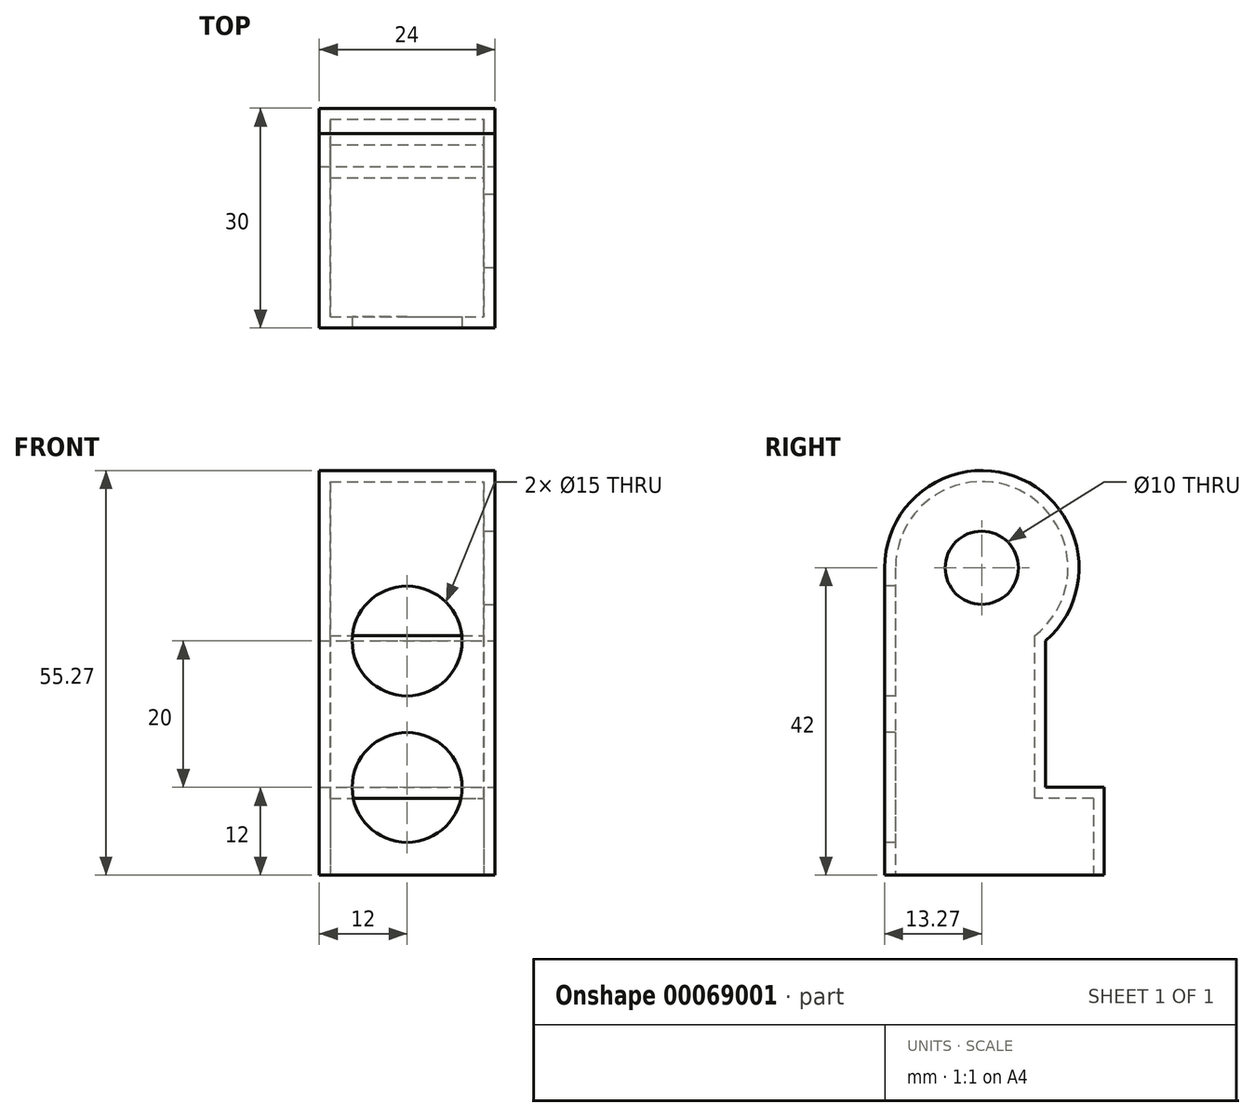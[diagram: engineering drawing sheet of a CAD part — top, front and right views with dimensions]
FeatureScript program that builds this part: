
annotation { "Feature Type Name" : "Feature", "Feature Type Description" : "" }
export const myFeature = defineFeature(function(context is Context, id is Id, definition is map)
    precondition{}
    {
        {
            var Q0;
            Q0=qCreatedBy(makeId("Right.planeOp"),FACE);
            var sketch = newSketch(context, id + "F0", { "sketchPlane" : qUnion([Q0])});
            skArc(sketch, "E0", {"start": v(8.73, -10) * mm, "mid": v(5.5, 12.08) * mm, "end": v(-13.27, 0) * mm});
            skLineSegment(sketch, "E1", {"start": v(-13.27, 0) * mm, "end": v(-13.27, -42) * mm});
            skLineSegment(sketch, "E2", {"start": v(-13.27, -42) * mm, "end": v(16.73, -42) * mm});
            skLineSegment(sketch, "E3", {"start": v(16.73, -30) * mm, "end": v(16.73, -42) * mm});
            skLineSegment(sketch, "E4", {"start": v(16.73, -30) * mm, "end": v(8.73, -30) * mm});
            skLineSegment(sketch, "E5", {"start": v(8.73, -30) * mm, "end": v(8.73, -10) * mm});
            skSolve(sketch);
        }
        {
            var Q0;
            Q0=makeQuery(id+"F0.imprint","IMPRINT",FACE,{"disambiguationData":[TD([[makeQuery(id+"F0.imprint","IMPRINT",EDGE,{"derivedFrom":sQuery(id+"F0.wireOp",EDGE,"E0")}),1.0]])]});
            extrude(context, id + "F1", {"entities" : qUnion([Q0]), "depth" : 24 * mm});
        }
        {
            var Q0;
            Q0=makeQuery(id+"F1.opExtrude","SWEPT_FACE",FACE,{"disambiguationData":[OSD([sQuery(id+"F0.wireOp",EDGE,"E2")])]});
            shell(context, id + "F2", {"entities" : qUnion([Q0]), "thickness" : 1.5 * mm});
        }
        {
            var Q0;
            Q0=makeQuery(id+"F1.opExtrude","CAP_FACE",FACE,{"disambiguationData":[OSD([sQuery(id+"F0.wireOp",EDGE,"E0"),sQuery(id+"F0.wireOp",EDGE,"E1"),sQuery(id+"F0.wireOp",EDGE,"E2"),sQuery(id+"F0.wireOp",EDGE,"E3"),sQuery(id+"F0.wireOp",EDGE,"E4"),sQuery(id+"F0.wireOp",EDGE,"E5")])],"isStart":true});
            var sketch = newSketch(context, id + "F3", { "sketchPlane" : qUnion([Q0])});
            skCircle(sketch, "E6", {"center": v(0, 0) * mm, "radius": 5 * mm});
            skSolve(sketch);
        }
        {
            var Q0;
            Q0=qSketchRegion(id+"F3",true);
            extrude(context, id + "F4", {"entities" : qUnion([Q0]), "operationType" : NewBodyOperationType.REMOVE, "oppositeDirection" : true, "depth" : 5 * mm});
        }
        {
            var Q0;
            Q0=makeQuery(id+"F1.opExtrude","SWEPT_FACE",FACE,{"disambiguationData":[OSD([sQuery(id+"F0.wireOp",EDGE,"E1")])]});
            var sketch = newSketch(context, id + "F5", { "sketchPlane" : qUnion([Q0])});
            skCircle(sketch, "E7", {"center": v(12, -10) * mm, "radius": 7.5 * mm});
            skCircle(sketch, "E8", {"center": v(12, -30) * mm, "radius": 7.5 * mm});
            skSolve(sketch);
        }
        {
            var Q0;
            Q0=qSketchRegion(id+"F5",true);
            extrude(context, id + "F6", {"entities" : qUnion([Q0]), "operationType" : NewBodyOperationType.REMOVE, "oppositeDirection" : true, "depth" : 5 * mm});
        }
        {
            var Q0;
            Q0=makeQuery(id+"F1.opExtrude","SWEPT_BODY",BODY,{"disambiguationData":[OSD([sQuery(id+"F0.wireOp",EDGE,"E0"),sQuery(id+"F0.wireOp",EDGE,"E1"),sQuery(id+"F0.wireOp",EDGE,"E2"),sQuery(id+"F0.wireOp",EDGE,"E3"),sQuery(id+"F0.wireOp",EDGE,"E4"),sQuery(id+"F0.wireOp",EDGE,"E5")])]});
            var Q1;
            Q1=makeQuery(id+"F1.opExtrude","CAP_FACE",FACE,{"disambiguationData":[OSD([sQuery(id+"F0.wireOp",EDGE,"E0"),sQuery(id+"F0.wireOp",EDGE,"E1"),sQuery(id+"F0.wireOp",EDGE,"E2"),sQuery(id+"F0.wireOp",EDGE,"E3"),sQuery(id+"F0.wireOp",EDGE,"E4"),sQuery(id+"F0.wireOp",EDGE,"E5")])],"isStart":true});
            mirror(context, id + "F7", {"entities" : qUnion([Q0]), "mirrorPlane" : qUnion([Q1])});
        }
        {
            var Q0;
            Q0=makeQuery(id+"F1.opExtrude","SWEPT_BODY",BODY,{"disambiguationData":[OSD([sQuery(id+"F0.wireOp",EDGE,"E0"),sQuery(id+"F0.wireOp",EDGE,"E1"),sQuery(id+"F0.wireOp",EDGE,"E2"),sQuery(id+"F0.wireOp",EDGE,"E3"),sQuery(id+"F0.wireOp",EDGE,"E4"),sQuery(id+"F0.wireOp",EDGE,"E5")])]});
            deleteBodies(context, id + "F8", {"entities" : qUnion([Q0])});
        }
    });
